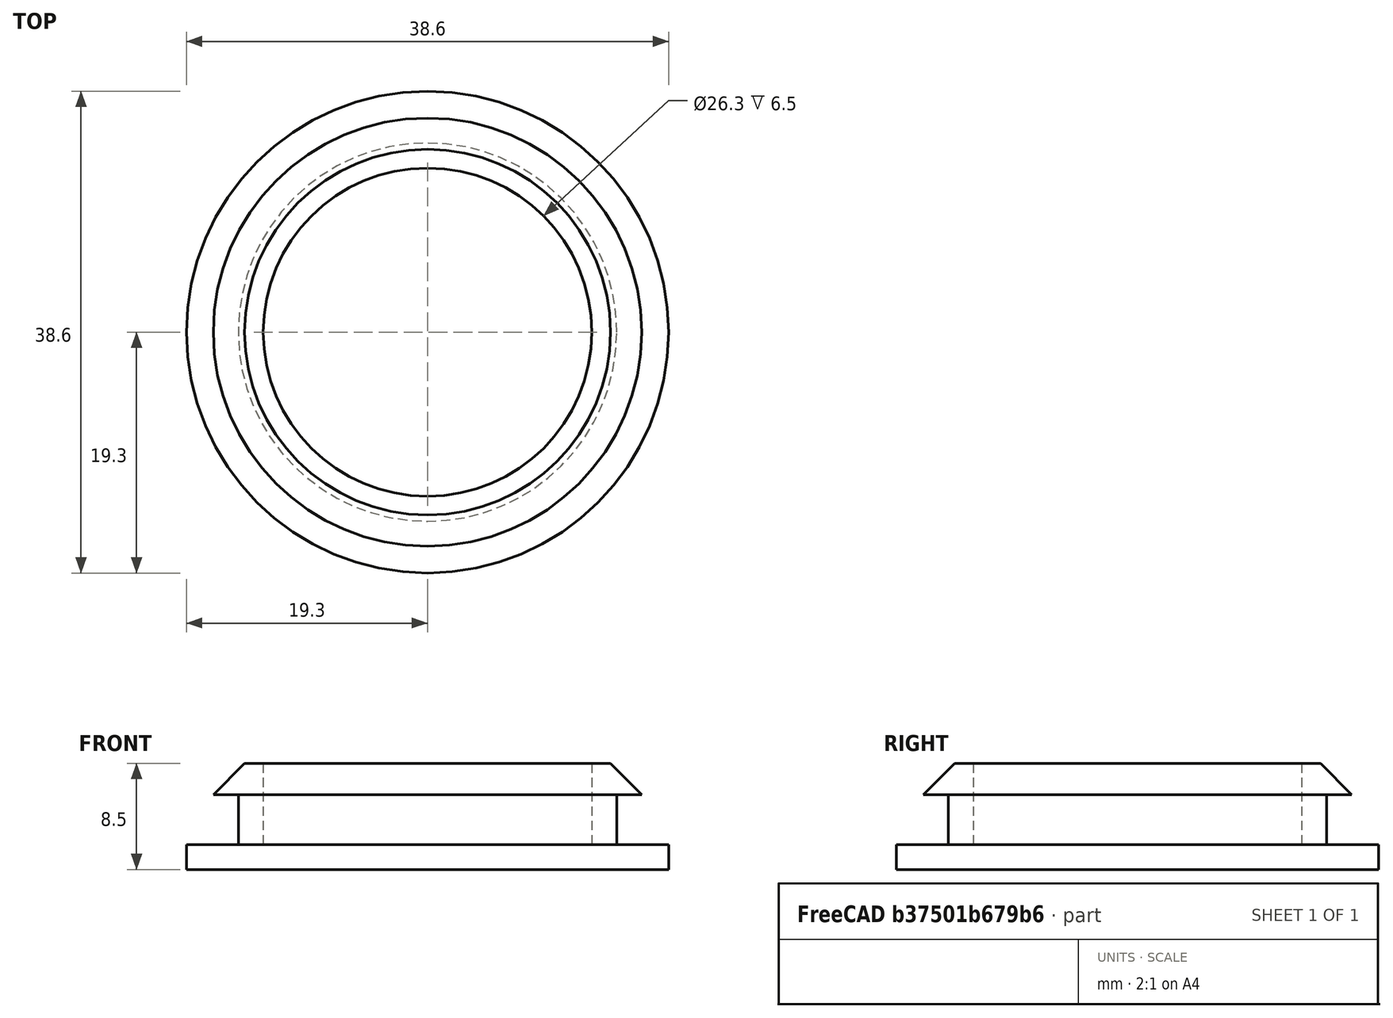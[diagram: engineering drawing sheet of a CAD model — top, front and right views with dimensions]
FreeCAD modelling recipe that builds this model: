
FCSTD DOCUMENT  (FreeCAD 0.20R29177 +426 (Git))
Label: car_seat_bolt_cover_30mm
License: Creative Commons
LicenseURL: http://creativecommons.org/licenses/by/3.0/
objects: Sketcher::SketchObject×1, PartDesign::Revolution×1, PartDesign::Body×1, Mesh::Feature×1
note: 4 computed .brp shape members not serialized (recipe doc carries the construction recipe); baked Part::Feature solids carry a one-line shape summary decoded from their .brp

FEATURE [Sketcher::SketchObject] Sketch
  FullyConstrained = true
  MapMode = 5
  Placement = pos=(0,0,0) rot=(1,0,0;1.5708rad)
  Support = -> [XZ_Plane]
  expr: Constraints[12] = 38.6 / 2
  expr: Constraints[15] = 30.3 / 2
  sketch-geometry (10):
    g0: LineSegment StartX=-19.3 StartY=0 StartZ=0 EndX=-19.3 EndY=2 EndZ=0
    g1: LineSegment StartX=-19.3 StartY=2 StartZ=0 EndX=-15.15 EndY=2 EndZ=0
    g2: LineSegment StartX=-15.15 StartY=2 StartZ=0 EndX=-15.15 EndY=6 EndZ=0
    g3: LineSegment StartX=-19.3 StartY=0 StartZ=0 EndX=0 EndY=0 EndZ=0
    g4: LineSegment StartX=0 StartY=0 StartZ=0 EndX=0 EndY=2 EndZ=0
    g5: LineSegment StartX=0 StartY=2 StartZ=0 EndX=-13.15 EndY=2 EndZ=0
    g6: LineSegment StartX=-15.15 StartY=6 StartZ=0 EndX=-17.15 EndY=6 EndZ=0
    g7: LineSegment StartX=-17.15 StartY=6 StartZ=0 EndX=-14.65 EndY=8.5 EndZ=0
    g8: LineSegment StartX=-14.65 StartY=8.5 StartZ=0 EndX=-13.15 EndY=8.5 EndZ=0
    g9: LineSegment StartX=-13.15 StartY=8.5 StartZ=0 EndX=-13.15 EndY=2 EndZ=0
  constraints (29):
    c: Vertical(g0)
    c: Coincident(g0,g1)
    c: Horizontal(g1)
    c: Coincident(g1,g2)
    c: Vertical(g2)
    c: Horizontal(g3)
    c: Coincident(g3,g4)
    c: Coincident(g4,g5)
    c: Horizontal(g5)
    c: Coincident(g3,g0)
    c: Coincident(g3,g-1)
    c: Vertical(g4)
    c: DistanceX(g3,g3) = 19.3
    c: DistanceY(g0,g0) = 2
    c: Equal(g4,g0)
    c: DistanceX(g1,g4) = 15.15
    c: DistanceY(g2,g2) = 4
    c: DistanceX(g1,g5) = 2
    c: Horizontal(g6)
    c: Coincident(g6,g7)
    c: Coincident(g6,g2)
    c: DistanceX(g6,g6) = 2
    c: Coincident(g7,g8)
    c: Horizontal(g8)
    c: Coincident(g8,g9)
    c: Vertical(g9)
    c: Coincident(g9,g5)
    c: Angle(g6,g7) = 0.785398
    c: DistanceX(g8,g8) = 1.5
FEATURE [PartDesign::Revolution] Revolution
  Angle = 360
  Axis = (0,2e-16,1)
  Base = (0,0,0)
  Placement = pos=(0,0,0) rot=(1,0,0;1.5708rad)
  Profile = -> Sketch
  ReferenceAxis = -> Sketch [V_Axis]
FEATURE [PartDesign::Body] Body
  Group = -> [Sketch,Revolution]
  Origin = -> Origin
  Tip = -> Revolution
FEATURE [Mesh::Feature] Mesh  label="Revolution (Meshed)"
